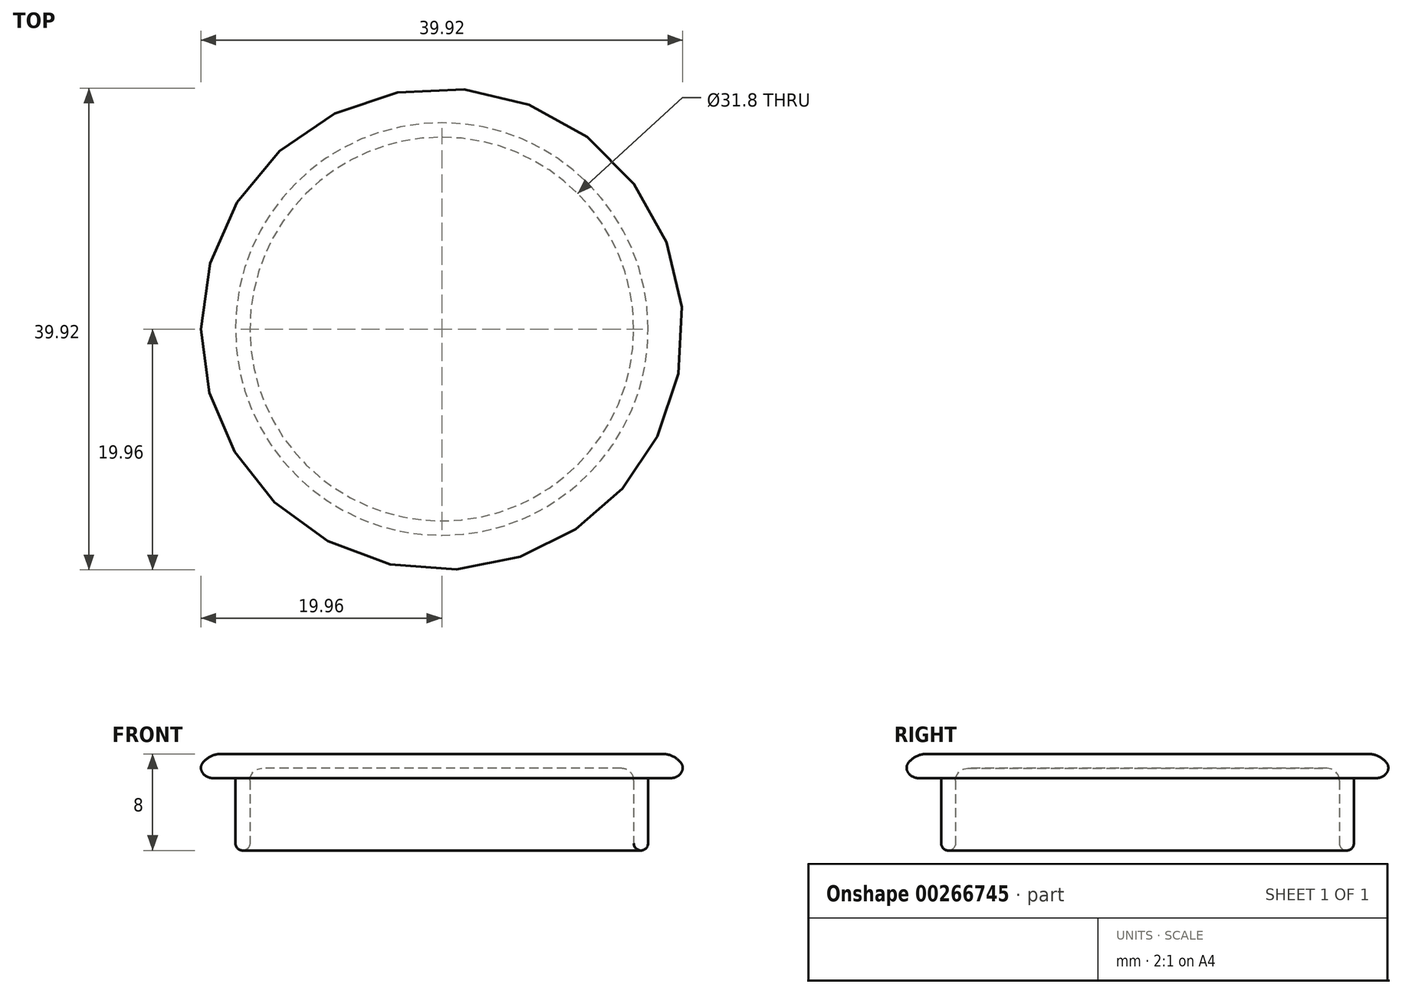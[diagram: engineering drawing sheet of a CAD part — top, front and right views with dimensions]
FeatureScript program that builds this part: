
annotation { "Feature Type Name" : "Feature", "Feature Type Description" : "" }
export const myFeature = defineFeature(function(context is Context, id is Id, definition is map)
    precondition{}
    {
        {
            var Q0;
            Q0=qCreatedBy(makeId("Top.planeOp"),FACE);
            var sketch = newSketch(context, id + "F0", { "sketchPlane" : qUnion([Q0])});
            skCircle(sketch, "E0", {"center": v(0, 0) * mm, "radius": 17.1 * mm});
            skSolve(sketch);
        }
        {
            var Q0;
            Q0=makeQuery(id+"F0.imprint","IMPRINT",FACE,{"disambiguationData":[TD([[makeQuery(id+"F0.imprint","IMPRINT",EDGE,{"derivedFrom":sQuery(id+"F0.wireOp",EDGE,"E0")}),1.0]])]});
            extrude(context, id + "F1", {"entities" : qUnion([Q0]), "depth" : 6 * mm});
        }
        {
            var Q0;
            Q0=makeQuery(id+"F1.opExtrude","CAP_FACE",FACE,{"disambiguationData":[OSD([sQuery(id+"F0.wireOp",EDGE,"E0")])],"isStart":false});
            var sketch = newSketch(context, id + "F2", { "sketchPlane" : qUnion([Q0])});
            skCircle(sketch, "E1", {"center": v(0, 0) * mm, "radius": 20 * mm});
            skSolve(sketch);
        }
        {
            var Q0;
            Q0=makeQuery(id+"F2.imprint","IMPRINT",FACE,{"disambiguationData":[TD([[makeQuery(id+"F2.imprint","IMPRINT",EDGE,{"derivedFrom":makeQuery(id+"F1.opExtrude","CAP_EDGE",EDGE,{"disambiguationData":[OSD([sQuery(id+"F0.wireOp",EDGE,"E0")])],"isStart":false})}),1.0]])]});
            var Q1;
            Q1=makeQuery(id+"F2.imprint","IMPRINT",FACE,{"disambiguationData":[TD([[makeQuery(id+"F2.imprint","IMPRINT",EDGE,{"derivedFrom":sQuery(id+"F2.wireOp",EDGE,"E1")}),1.0]])]});
            extrude(context, id + "F3", {"entities" : qUnion([Q0, Q1]), "operationType" : NewBodyOperationType.ADD, "depth" : 2 * mm});
        }
        {
            var Q0;
            Q0=makeQuery(id+"F1.opExtrude","CAP_FACE",FACE,{"disambiguationData":[OSD([sQuery(id+"F0.wireOp",EDGE,"E0")])],"isStart":true});
            shell(context, id + "F4", {"entities" : qUnion([Q0]), "thickness" : 1.2 * mm});
        }
        {
            var Q0;
            {var subQ0=sQuery(id+"F0.wireOp",EDGE,"E0");Q0=makeQuery(id+"F4.opShell","OFFSET_EDGE",EDGE,{"disambiguationData":[OSD([subQ0]),TDD([makeQuery(id+"F1.opExtrude","CAP_EDGE",EDGE,{"disambiguationData":[OSD([subQ0])],"isStart":true})])]});}
            var Q1;
            Q1=makeQuery(id+"F1.opExtrude","CAP_EDGE",EDGE,{"disambiguationData":[OSD([sQuery(id+"F0.wireOp",EDGE,"E0")])],"isStart":true});
            fillet(context, id + "F5", {"entities" : qUnion([Q0, Q1]), "radius" : .6 * mm, "tangentPropagation" : true, "allowEdgeOverflow" : false});
        }
        {
            var Q0;
            Q0=makeQuery(id+"F1.opExtrude","CAP_EDGE",EDGE,{"disambiguationData":[OSD([sQuery(id+"F0.wireOp",EDGE,"E0")])],"isStart":false});
            var Q1;
            Q1=makeQuery(id+"F3.opExtrude","CAP_EDGE",EDGE,{"disambiguationData":[OSD([sQuery(id+"F2.wireOp",EDGE,"E1")])],"isStart":true});
            var Q2;
            Q2=makeQuery(id+"F4.opShell","TWEAK_EDGE",EDGE,{"derivedFrom":[makeQuery(id+"F1.opExtrude","SWEPT_FACE",FACE,{"disambiguationData":[OSD([sQuery(id+"F0.wireOp",EDGE,"E0")])]}),makeQuery(id+"F3.opExtrude","CAP_FACE",FACE,{"disambiguationData":[OSD([sQuery(id+"F2.wireOp",EDGE,"E1")])],"isStart":false})]});
            fillet(context, id + "F6", {"entities" : qUnion([Q0, Q1, Q2]), "radius" : 1 * mm, "tangentPropagation" : true, "allowEdgeOverflow" : false});
        }
        {
            var Q0;
            Q0=makeQuery(id+"F3.opExtrude","CAP_EDGE",EDGE,{"disambiguationData":[OSD([sQuery(id+"F2.wireOp",EDGE,"E1")])],"isStart":false});
            fillet(context, id + "F7", {"entities" : qUnion([Q0]), "radius" : 2 * mm, "allowEdgeOverflow" : false});
        }
        {
            var Q0;
            {var subQ0=sQuery(id+"F2.wireOp",EDGE,"E1");Q0=makeQuery(id+"F7.opFillet","BLEND_EDGE",EDGE,{"blendedFrom":[makeQuery(id+"F3.opExtrude","CAP_EDGE",EDGE,{"disambiguationData":[OSD([subQ0])],"isStart":false}),makeQuery(id+"F6.opFillet","BLEND_FACE",FACE,{"disambiguationData":[OSD([subQ0])]})],"blendedInto":[makeQuery(id+"F6.opFillet","BLEND_FACE",FACE,{"disambiguationData":[OSD([subQ0])]})]});}
            fillet(context, id + "F8", {"entities" : qUnion([Q0]), "radius" : .7 * mm, "tangentPropagation" : true, "allowEdgeOverflow" : false});
        }
    });
